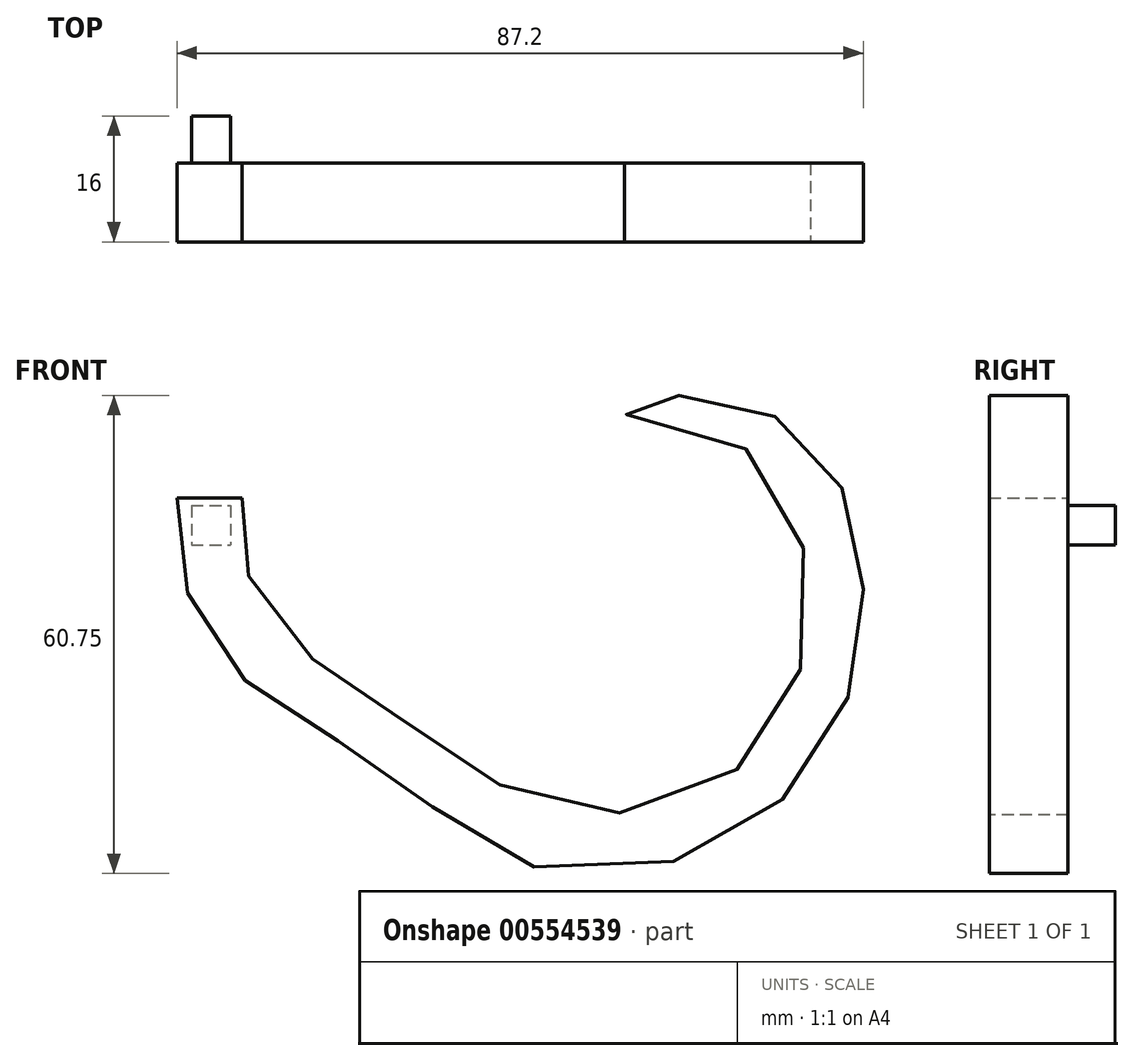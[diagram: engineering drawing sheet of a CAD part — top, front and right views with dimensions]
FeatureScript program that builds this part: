
annotation { "Feature Type Name" : "Feature", "Feature Type Description" : "" }
export const myFeature = defineFeature(function(context is Context, id is Id, definition is map)
    precondition{}
    {
        {
            var Q0;
            Q0=qCreatedBy(makeId("Front.planeOp"),FACE);
            var sketch = newSketch(context, id + "F0", { "sketchPlane" : qUnion([Q0])});
            skLineSegment(sketch, "E0", {"start": v(-43.88, 27.1) * mm, "end": v(-35.58, 27.1) * mm});
            skFitSpline(sketch, "E1", {"points": [v(-35.58, 27.1) * mm, v(-35.58, 22) * mm, v(-33.88, 14.97) * mm, v(-26.64, 6.68) * mm, v(-17.07, 0) * mm, v(-6.85, -6.52) * mm, v(4.42, -12.69) * mm, v(21.23, -10.77) * mm, v(30.8, -3.75) * mm, v(36.34, 9.87) * mm, v(35.06, 23.27) * mm, v(28.04, 33.48) * mm, v(13.36, 37.53) * mm, v(13.41, 39.22) * mm, v(17.43, 40.1) * mm, v(25.27, 39.6) * mm, v(34.38, 36.18) * mm, v(40.2, 29.22) * mm, v(43.1, 18.34) * mm, v(43.04, 10.81) * mm, v(39.43, -3.48) * mm, v(30.4, -13.26) * mm, v(16.26, -19.88) * mm, v(-1.65, -18.83) * mm, v(-12.03, -11.6) * mm, v(-22.4, -4.38) * mm, v(-32.34, 1.48) * mm, v(-40.2, 9.98) * mm, v(-43.35, 18.4) * mm, v(-43.88, 27.1) * mm], "startDerivative": vector(-7.27, -207.9) * mm, "endDerivative": vector(-2.2, 278.65) * mm});
            skPoint(sketch, "E2.middle", {"position": v(-39.83, 23.6) * mm});
            skSolve(sketch);
        }
        {
            var Q0;
            Q0=makeQuery(id+"F0.imprint","IMPRINT",FACE,{"disambiguationData":[TD([[makeQuery(id+"F0.imprint","IMPRINT",EDGE,{"derivedFrom":sQuery(id+"F0.wireOp",EDGE,"E0")}),-1.0]])]});
            extrude(context, id + "F1", {"entities" : qUnion([Q0]), "depth" : 10 * mm, "offsetDistance" : 25 * mm});
        }
        {
            var Q0;
            Q0=makeQuery(id+"F1.opExtrude","CAP_FACE",FACE,{"disambiguationData":[OSD([sQuery(id+"F0.wireOp",EDGE,"E0"),sQuery(id+"F0.wireOp",EDGE,"E1")])],"isStart":true});
            var sketch = newSketch(context, id + "F2", { "sketchPlane" : qUnion([Q0])});
            skLineSegment(sketch, "E3.bottom", {"start": v(42.03, 26.1) * mm, "end": v(37.03, 26.1) * mm});
            skLineSegment(sketch, "E3.top", {"start": v(42.03, 21.1) * mm, "end": v(37.03, 21.1) * mm});
            skLineSegment(sketch, "E3.left", {"start": v(42.03, 26.1) * mm, "end": v(42.03, 21.1) * mm});
            skLineSegment(sketch, "E3.right", {"start": v(37.03, 26.1) * mm, "end": v(37.03, 21.1) * mm});
            skPoint(sketch, "E3.middle", {"position": v(39.53, 23.6) * mm});
            skSolve(sketch);
        }
        {
            var Q0;
            Q0=makeQuery(id+"F2.imprint","IMPRINT",FACE,{"disambiguationData":[TD([[makeQuery(id+"F2.imprint","IMPRINT",EDGE,{"derivedFrom":sQuery(id+"F2.wireOp",EDGE,"E3.bottom")}),1.0]])]});
            extrude(context, id + "F3", {"entities" : qUnion([Q0]), "operationType" : NewBodyOperationType.ADD, "depth" : 6 * mm, "offsetDistance" : 25 * mm});
        }
    });
